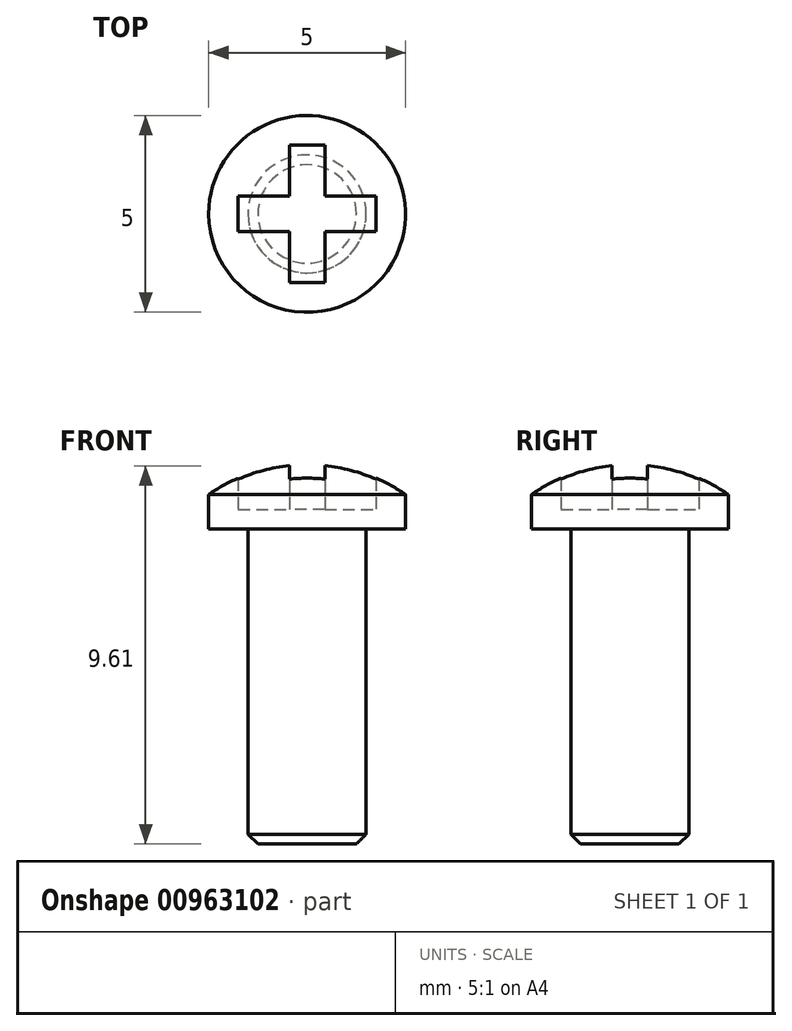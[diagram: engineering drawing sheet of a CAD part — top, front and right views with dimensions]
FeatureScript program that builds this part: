
annotation { "Feature Type Name" : "Feature", "Feature Type Description" : "" }
export const myFeature = defineFeature(function(context is Context, id is Id, definition is map)
    precondition{}
    {
        {
            var Q0;
            Q0=qCreatedBy(makeId("Front.planeOp"),FACE);
            var sketch = newSketch(context, id + "F0", { "sketchPlane" : qUnion([Q0])});
            skLineSegment(sketch, "E0", {"start": v(-1.5, 0) * mm, "end": v(-2.5, 0) * mm});
            skLineSegment(sketch, "E1", {"start": v(-2.5, 0) * mm, "end": v(-2.5, 0.88) * mm});
            skLineSegment(sketch, "E2", {"start": v(-1.5, 0) * mm, "end": v(-1.5, -8) * mm});
            skLineSegment(sketch, "E3", {"start": v(-1.5, -8) * mm, "end": v(0, -8) * mm});
            skLineSegment(sketch, "E4", {"start": v(0, -8) * mm, "end": v(0, 1.66) * mm});
            skArc(sketch, "E5", {"start": v(0, 1.66) * mm, "mid": v(-1.3, 1.46) * mm, "end": v(-2.5, 0.88) * mm});
            skSolve(sketch);
        }
        {
            var Q0;
            Q0=qSketchRegion(id+"F0",true);
            var Q1;
            Q1=sQuery(id+"F0.wireOp",EDGE,"E4");
            revolve(context, id + "F1", {"surfaceOperationType" : NewSurfaceOperationType.NEW, "entities" : qUnion([Q0]), "axis" : qUnion([Q1]), "revolveType" : RevolveType.FULL});
        }
        {
            var Q0;
            Q0=makeQuery(id+"F1.opRevolve","SWEPT_EDGE",EDGE,{"disambiguationData":[OSD([sQuery(id+"F0.wireOp",EDGE,"E2"),sQuery(id+"F0.wireOp",EDGE,"E3")])]});
            chamfer(context, id + "F2", {"entities" : qUnion([Q0]), "width" : 0.25 * mm, "tangentPropagation" : true});
        }
        {
            var Q0;
            Q0=qCreatedBy(makeId("Top.planeOp"),FACE);
            cPlane(context, id + "F3", {"entities" : qUnion([Q0]), "cplaneType" : CPlaneType.OFFSET, "offset" : 0.5 * mm, "width" : 150 * mm, "height" : 150 * mm});
        }
        {
            var Q0;
            Q0=qCreatedBy(id+"F3.planeOp",FACE);
            var sketch = newSketch(context, id + "F4", { "sketchPlane" : qUnion([Q0])});
            skLineSegment(sketch, "E6.bottom", {"start": v(-1.75, 0.45) * mm, "end": v(-0.45, 0.45) * mm});
            skLineSegment(sketch, "E6.top", {"start": v(-1.75, -0.45) * mm, "end": v(-0.45, -0.45) * mm});
            skLineSegment(sketch, "E6.left", {"start": v(-1.75, 0.45) * mm, "end": v(-1.75, -0.45) * mm});
            skLineSegment(sketch, "E6.right", {"start": v(1.75, 0.45) * mm, "end": v(1.75, -0.45) * mm});
            skLineSegment(sketch, "E7.bottom", {"start": v(0.45, -1.75) * mm, "end": v(-0.45, -1.75) * mm});
            skLineSegment(sketch, "E7.top", {"start": v(0.45, 1.75) * mm, "end": v(-0.45, 1.75) * mm});
            skLineSegment(sketch, "E7.left", {"start": v(0.45, -1.75) * mm, "end": v(0.45, -0.45) * mm});
            skLineSegment(sketch, "E7.right", {"start": v(-0.45, -1.75) * mm, "end": v(-0.45, -0.45) * mm});
            skLineSegment(sketch, "E8", {"start": v(-0.45, 1.75) * mm, "end": v(0.45, -1.75) * mm, "construction": true});
            skLineSegment(sketch, "E9", {"start": v(1.75, 0.45) * mm, "end": v(-1.75, -0.45) * mm, "construction": true});
            skLineSegment(sketch, "E10.trimOffspring", {"start": v(0.45, 0.45) * mm, "end": v(1.75, 0.45) * mm});
            skLineSegment(sketch, "E11.trimOffspring", {"start": v(-0.45, 0.45) * mm, "end": v(-0.45, 1.75) * mm});
            skLineSegment(sketch, "E12.trimOffspring", {"start": v(0.45, -0.45) * mm, "end": v(1.75, -0.45) * mm});
            skLineSegment(sketch, "E13.trimOffspring", {"start": v(0.45, 0.45) * mm, "end": v(0.45, 1.75) * mm});
            skSolve(sketch);
        }
        {
            var Q0;
            Q0=qSketchRegion(id+"F4",true);
            extrude(context, id + "F5", {"entities" : qUnion([Q0]), "operationType" : NewBodyOperationType.REMOVE, "endBound" : BoundingType.UP_TO_NEXT, "depth" : 25 * mm, "offsetDistance" : 25 * mm});
        }
    });
